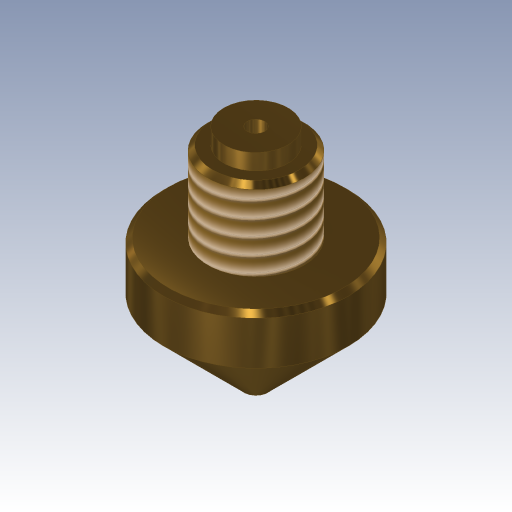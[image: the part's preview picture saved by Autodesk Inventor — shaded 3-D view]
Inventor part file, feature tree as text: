
AUTODESK INVENTOR PART (.ipt)
format: ipt  version: 2023.3 (Build 273359000, 359)  size: 208,896 bytes
history: native  units: in
note: dims shown in document units (in); Inventor stores cm internally (conversion verified against a paired STEP export)
features: revolve x1, thread x1, chamfer x1, sketch x1
ambient origin geometry x8: Origin, YZ Plane, XZ Plane, XY Plane, X Axis, Y Axis, Z Axis, Center Point
bodies: Body1 (feature_tree)
feature tree (4):
  revolve  "Umdrehung1"
  thread  "Gewinde1"  [1 undecoded]
  chamfer  "Fase1"  Distance=0.2362in
  sketch  "Skizze3"  dims[d9=0.4528in d11=0.2362in d12=0.1575in d13=0.0394in d15=0.0433in d16=360.0deg d17=0.5906in d18=0.0in d19=0.0118in d20=0.0787in d21=45.0deg d37=45.0deg d38=0.1181in d39=0.2362in]
note: 1 required parameter value undecoded (feature->parameter linkage not recoverable at this tier; creation-order binding heuristic only, values carry confidence <= 0.55)
